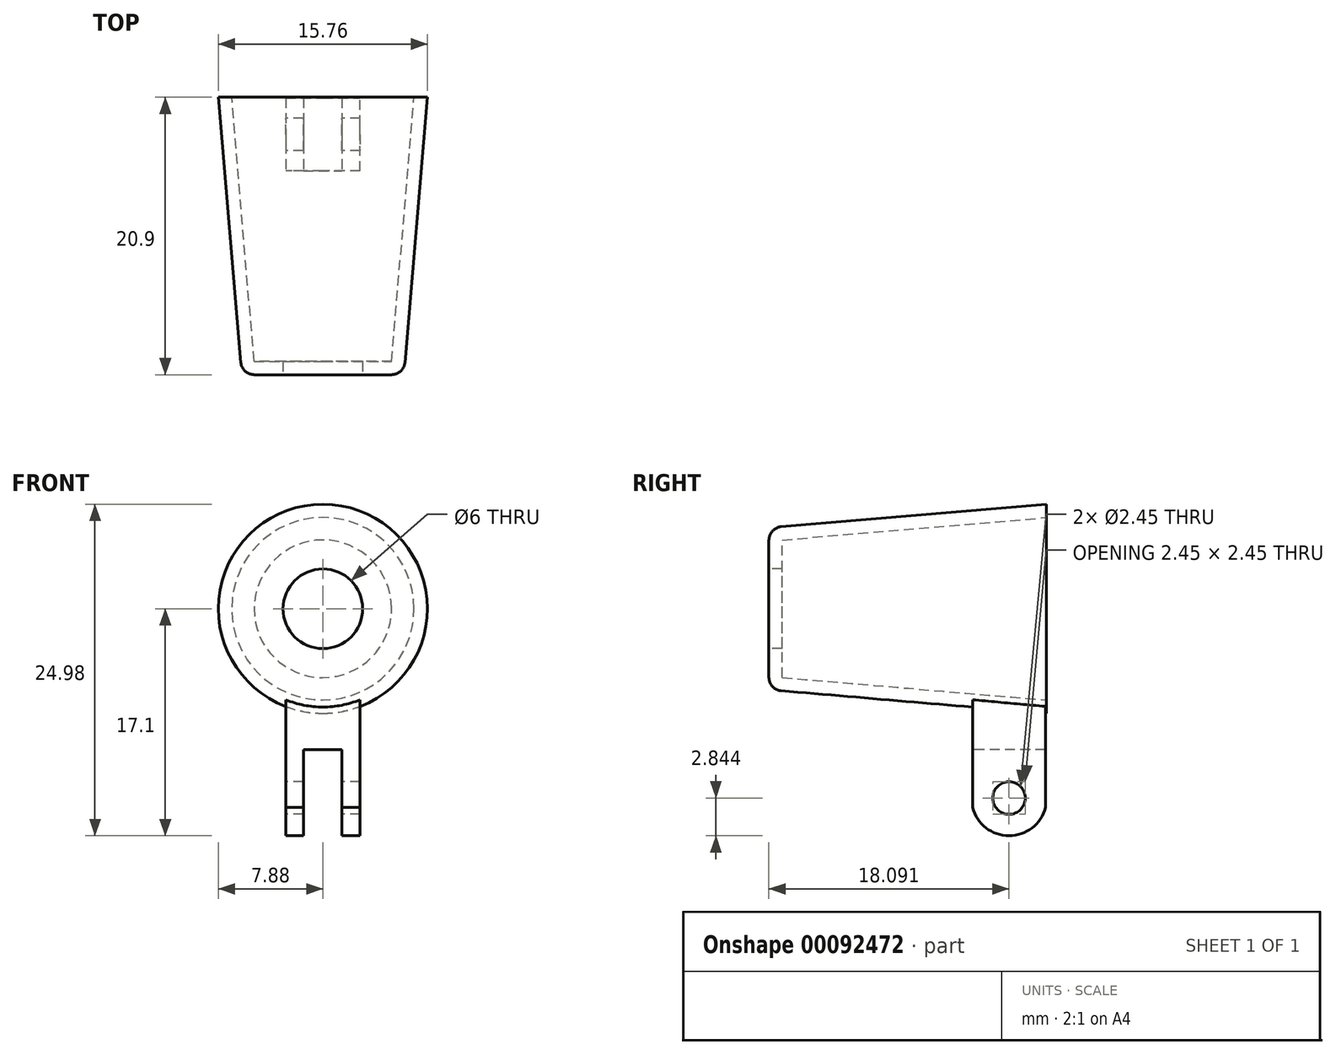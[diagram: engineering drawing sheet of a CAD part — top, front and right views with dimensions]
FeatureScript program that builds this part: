
annotation { "Feature Type Name" : "Feature", "Feature Type Description" : "" }
export const myFeature = defineFeature(function(context is Context, id is Id, definition is map)
    precondition{}
    {
        {
            var Q0;
            Q0=qCreatedBy(makeId("Front.planeOp"),FACE);
            var sketch = newSketch(context, id + "F0", { "sketchPlane" : qUnion([Q0])});
            skCircle(sketch, "E0", {"center": v(0, 0) * mm, "radius": 7.88 * mm});
            skSolve(sketch);
        }
        {
            var Q0;
            Q0=qCreatedBy(makeId("Front.planeOp"),FACE);
            cPlane(context, id + "F1", {"entities" : qUnion([Q0]), "cplaneType" : CPlaneType.OFFSET, "offset" : 20.9 * mm, "width" : 150 * mm, "height" : 150 * mm});
        }
        {
            var Q0;
            Q0=qCreatedBy(id+"F1.planeOp",FACE);
            var sketch = newSketch(context, id + "F2", { "sketchPlane" : qUnion([Q0])});
            skCircle(sketch, "E1", {"center": v(0, 0) * mm, "radius": 6.1 * mm});
            skSolve(sketch);
        }
        {
            var Q0;
            Q0=makeQuery(id+"F0.imprint","IMPRINT",FACE,{"disambiguationData":[TD([[makeQuery(id+"F0.imprint","IMPRINT",EDGE,{"derivedFrom":sQuery(id+"F0.wireOp",EDGE,"E0")}),1.0]])]});
            var Q1;
            Q1=makeQuery(id+"F2.imprint","IMPRINT",FACE,{"disambiguationData":[TD([[makeQuery(id+"F2.imprint","IMPRINT",EDGE,{"derivedFrom":sQuery(id+"F2.wireOp",EDGE,"E1")}),1.0]])]});
            loft(context, id + "F3", {"sheetProfilesArray" : [{ "sheetProfileEntities" : qUnion([Q0]) }, { "sheetProfileEntities" : qUnion([Q1]) }]});
        }
        {
            var Q0;
            Q0=makeQuery(id+"F3.opLoft","CAP_FACE",FACE,{"disambiguationData":[OSD([makeQuery(id+"F0.imprint","IMPRINT",FACE,{"disambiguationData":[TD([[makeQuery(id+"F0.imprint","IMPRINT",EDGE,{"derivedFrom":sQuery(id+"F0.wireOp",EDGE,"E0")}),1.0]])]})])],"isStart":true});
            shell(context, id + "F4", {"entities" : qUnion([Q0]), "thickness" : 1 * mm});
        }
        {
            var Q0;
            Q0=qCreatedBy(id+"F1.planeOp",FACE);
            var sketch = newSketch(context, id + "F5", { "sketchPlane" : qUnion([Q0])});
            skCircle(sketch, "E2", {"center": v(0, 0) * mm, "radius": 3 * mm});
            skSolve(sketch);
        }
        {
            var Q0;
            Q0=makeQuery(id+"F5.imprint","IMPRINT",FACE,{"disambiguationData":[TD([[makeQuery(id+"F5.imprint","IMPRINT",EDGE,{"derivedFrom":sQuery(id+"F5.wireOp",EDGE,"E2")}),1.0]])]});
            extrude(context, id + "F6", {"entities" : qUnion([Q0]), "operationType" : NewBodyOperationType.REMOVE, "oppositeDirection" : true, "depth" : 25 * mm, "symmetric" : true});
        }
        {
            var Q0;
            Q0=qCreatedBy(makeId("Right.planeOp"),FACE);
            var sketch = newSketch(context, id + "F7", { "sketchPlane" : qUnion([Q0])});
            skArc(sketch, "E3", {"start": v(-5.56, -14.97) * mm, "mid": v(-2.8, -17.1) * mm, "end": v(-0.06, -14.97) * mm});
            skCircle(sketch, "E4", {"center": v(-2.8, -14.26) * mm, "radius": 1.23 * mm});
            skLineSegment(sketch, "E5", {"start": v(-0.06, -14.97) * mm, "end": v(-0.06, -7.08) * mm});
            skLineSegment(sketch, "E6", {"start": v(-0.06, -7.08) * mm, "end": v(-5.56, -6.6) * mm});
            skLineSegment(sketch, "E7", {"start": v(-5.56, -6.6) * mm, "end": v(-5.56, -14.97) * mm});
            skSolve(sketch);
        }
        {
            var Q0;
            Q0 = qSketchRegion(id + "F7", true);
            extrude(context, id + "F8", {"entities" : qUnion([Q0]), "operationType" : NewBodyOperationType.ADD, "depth" : 5.6 * mm, "symmetric" : true});
        }
        {
            var Q0;
            Q0=qCreatedBy(id+"F1.planeOp",FACE);
            var sketch = newSketch(context, id + "F9", { "sketchPlane" : qUnion([Q0])});
            skLineSegment(sketch, "E8.bottom", {"start": v(1.44, -10.61) * mm, "end": v(-1.47, -10.61) * mm});
            skLineSegment(sketch, "E8.top", {"start": v(1.44, -17.9) * mm, "end": v(-1.47, -17.9) * mm});
            skLineSegment(sketch, "E8.left", {"start": v(1.44, -10.61) * mm, "end": v(1.44, -17.9) * mm});
            skLineSegment(sketch, "E8.right", {"start": v(-1.47, -10.61) * mm, "end": v(-1.47, -17.9) * mm});
            skSolve(sketch);
        }
        {
            var Q0;
            Q0 = qSketchRegion(id + "F9", true);
            extrude(context, id + "F10", {"entities" : qUnion([Q0]), "operationType" : NewBodyOperationType.REMOVE, "endBound" : BoundingType.THROUGH_ALL, "oppositeDirection" : true, "depth" : 25 * mm});
        }
        {
            var Q0;
            Q0=makeQuery(id+"F3.opLoft","MID_CAP_EDGE",EDGE,{"disambiguationData":[OSD([sQuery(id+"F0.wireOp",EDGE,"E0"),sQuery(id+"F2.wireOp",EDGE,"E1")])],"capPos":1.0});
            fillet(context, id + "F11", {"entities" : qUnion([Q0]), "radius" : 1 * mm, "tangentPropagation" : true, "allowEdgeOverflow" : false});
        }
    });
